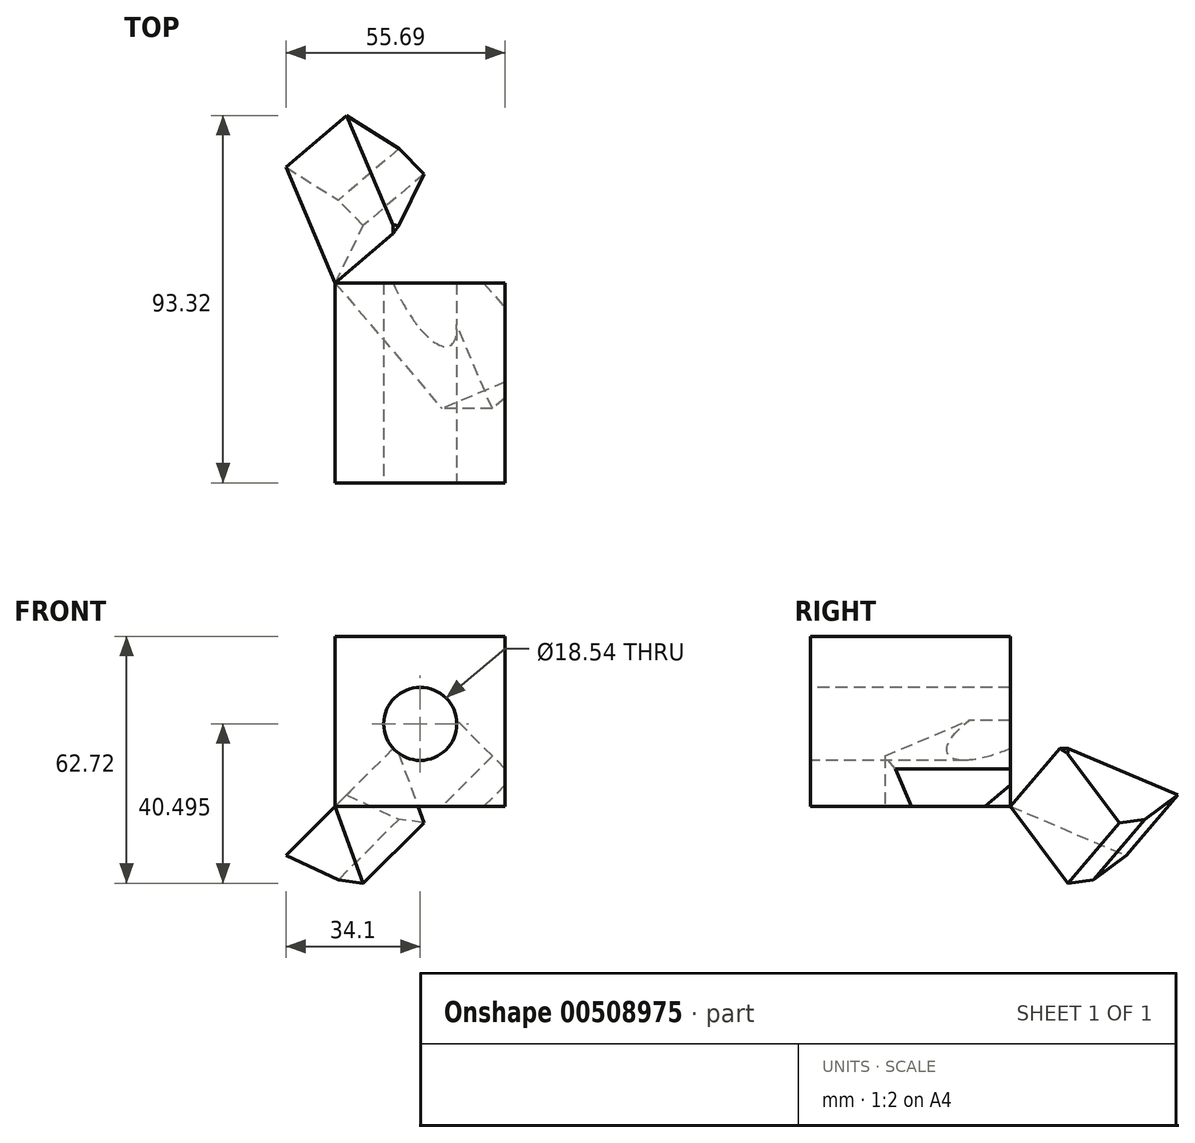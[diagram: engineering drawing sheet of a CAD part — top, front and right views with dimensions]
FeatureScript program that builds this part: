
annotation { "Feature Type Name" : "Feature", "Feature Type Description" : "" }
export const myFeature = defineFeature(function(context is Context, id is Id, definition is map)
    precondition{}
    {
        {
            var Q0;
            Q0=qCreatedBy(makeId("Front.planeOp"),FACE);
            var sketch = newSketch(context, id + "F0", { "sketchPlane" : qUnion([Q0])});
            skLineSegment(sketch, "E0.bottom", {"start": v(0, 0) * mm, "end": v(43.18, 0) * mm});
            skLineSegment(sketch, "E0.top", {"start": v(0, 43.18) * mm, "end": v(43.18, 43.18) * mm});
            skLineSegment(sketch, "E0.left", {"start": v(0, 0) * mm, "end": v(0, 43.18) * mm});
            skLineSegment(sketch, "E0.right", {"start": v(43.18, 0) * mm, "end": v(43.18, 43.18) * mm});
            skSolve(sketch);
        }
        {
            var Q0;
            Q0=makeQuery(id+"F0.imprint","IMPRINT",FACE,{"disambiguationData":[TD([[makeQuery(id+"F0.imprint","IMPRINT",EDGE,{"derivedFrom":sQuery(id+"F0.wireOp",EDGE,"E0.bottom")}),1.0]])]});
            extrude(context, id + "F1", {"entities" : qUnion([Q0]), "depth" : 50.8 * mm, "offsetDistance" : 25.4 * mm});
        }
        {
            var Q0;
            Q0=makeQuery(id+"F1.opExtrude","CAP_VERTEX",VERTEX,{"disambiguationData":[OSD([sQuery(id+"F0.wireOp",EDGE,"E0.bottom"),sQuery(id+"F0.wireOp",EDGE,"E0.right")])],"isStart":false});
            var Q1;
            Q1=makeQuery(id+"F1.opExtrude","CAP_VERTEX",VERTEX,{"disambiguationData":[OSD([sQuery(id+"F0.wireOp",EDGE,"E0.top"),sQuery(id+"F0.wireOp",EDGE,"E0.left")])],"isStart":false});
            var Q2;
            Q2=qCreatedBy(makeId("Origin.pointOp"),VERTEX);
            cPlane(context, id + "F2", {"entities" : qUnion([Q0, Q1, Q2]), "cplaneType" : CPlaneType.THREE_POINT, "offset" : 25.4 * mm, "oppositeDirection" : true, "width" : 152.4 * mm, "height" : 152.4 * mm});
        }
        {
            var Q0;
            Q0=qCreatedBy(id+"F2.planeOp",FACE);
            var sketch = newSketch(context, id + "F3", { "sketchPlane" : qUnion([Q0])});
            skLineSegment(sketch, "E1", {"start": v(-12.96, -13.84) * mm, "end": v(0, 0) * mm});
            skLineSegment(sketch, "E2", {"start": v(0, 0) * mm, "end": v(17.03, -18.86) * mm});
            skLineSegment(sketch, "E3", {"start": v(17.03, -18.86) * mm, "end": v(36.85, -5.4) * mm});
            skLineSegment(sketch, "E4", {"start": v(36.85, -5.4) * mm, "end": v(57.98, -14.18) * mm});
            skLineSegment(sketch, "E5", {"start": v(57.98, -14.18) * mm, "end": v(64.33, -5.59) * mm});
            skLineSegment(sketch, "E6.0", {"start": v(0, 0) * mm, "end": v(34.35, 0) * mm});
            skLineSegment(sketch, "E7.0", {"start": v(34.35, 0) * mm, "end": v(14.4, -27.97) * mm});
            skSolve(sketch);
        }
        {
            var Q0;
            Q0 = qSketchRegion(id + "F3", true);
            extrude(context, id + "F4", {"entities" : qUnion([Q0]), "operationType" : NewBodyOperationType.ADD, "depth" : 25.4 * mm, "offsetDistance" : 25.4 * mm});
        }
        {
            var Q0;
            Q0=makeQuery(id+"F4.opExtrude","CAP_VERTEX",VERTEX,{"disambiguationData":[OSD([sQuery(id+"F3.wireOp",EDGE,"E2"),sQuery(id+"F3.wireOp",EDGE,"E6.0")])],"isStart":false});
            var Q1;
            Q1=makeQuery(id+"F4.opExtrude","CAP_VERTEX",VERTEX,{"disambiguationData":[OSD([sQuery(id+"F3.wireOp",EDGE,"E6.0"),sQuery(id+"F3.wireOp",EDGE,"E7.0")])],"isStart":true});
            var Q2;
            Q2=makeQuery(id+"F1.opExtrude","CAP_VERTEX",VERTEX,{"disambiguationData":[OSD([sQuery(id+"F0.wireOp",EDGE,"E0.top"),sQuery(id+"F0.wireOp",EDGE,"E0.right")])],"isStart":true});
            cPlane(context, id + "F5", {"entities" : qUnion([Q0, Q1, Q2]), "cplaneType" : CPlaneType.THREE_POINT, "offset" : 25.4 * mm, "width" : 152.4 * mm, "height" : 152.4 * mm});
        }
        {
            var Q0;
            Q0=qCreatedBy(id+"F5.planeOp",FACE);
            var sketch = newSketch(context, id + "F6", { "sketchPlane" : qUnion([Q0])});
            skCircle(sketch, "E8", {"center": v(-22.34, 27.43) * mm, "radius": 12.7 * mm});
            skLineSegment(sketch, "E9.0", {"start": v(-32.74, 0) * mm, "end": v(-45.03, 38.85) * mm});
            skLineSegment(sketch, "E10.0", {"start": v(-12.3, 38.85) * mm, "end": v(-45.03, 38.85) * mm});
            skLineSegment(sketch, "E11", {"start": v(-45.03, 38.85) * mm, "end": v(-22.34, 27.43) * mm, "construction": true});
            skSolve(sketch);
        }
        {
            var Q0;
            {var subQ0=sQuery(id+"F6.wireOp",EDGE,"E10.0");var subQ1=sQuery(id+"F6.wireOp",EDGE,"E8");var subQ2=makeQuery(id+"F6.imprint","INTERSECT",VERTEX,{"disambiguationData":[OD(0.0)],"derivedFrom":[subQ1,subQ0]});Q0=makeQuery(id+"F6.imprint","IMPRINT",FACE,{"disambiguationData":[TD([[makeQuery(id+"F6.imprint","IMPRINT",EDGE,{"disambiguationData":[TD([[subQ2,1.0]])],"derivedFrom":subQ1}),1.0]])]});}
            extrude(context, id + "F7", {"entities" : qUnion([Q0]), "operationType" : NewBodyOperationType.REMOVE, "oppositeDirection" : true, "depth" : 24.38 * mm, "offsetDistance" : 25.4 * mm});
        }
        {
            var Q0;
            Q0=makeQuery(id+"F1.opExtrude","CAP_VERTEX",VERTEX,{"disambiguationData":[OSD([sQuery(id+"F0.wireOp",EDGE,"E0.bottom"),sQuery(id+"F0.wireOp",EDGE,"E0.right")])],"isStart":false});
            var Q1;
            Q1=qCreatedBy(makeId("Origin.pointOp"),VERTEX);
            var Q2;
            Q2=makeQuery(id+"F1.opExtrude","CAP_VERTEX",VERTEX,{"disambiguationData":[OSD([sQuery(id+"F0.wireOp",EDGE,"E0.top"),sQuery(id+"F0.wireOp",EDGE,"E0.right")])],"isStart":true});
            cPlane(context, id + "F8", {"entities" : qUnion([Q0, Q1, Q2]), "cplaneType" : CPlaneType.THREE_POINT, "offset" : 25.4 * mm, "width" : 152.4 * mm, "height" : 152.4 * mm});
        }
        {
            var Q0;
            Q0=qCreatedBy(id+"F8.planeOp",FACE);
            var sketch = newSketch(context, id + "F9", { "sketchPlane" : qUnion([Q0])});
            skLineSegment(sketch, "E12.bottom", {"start": v(37.27, 37.27) * mm, "end": v(0, 37.27) * mm});
            skLineSegment(sketch, "E12.top", {"start": v(37.27, 0) * mm, "end": v(0, 0) * mm});
            skLineSegment(sketch, "E12.left", {"start": v(37.27, 37.27) * mm, "end": v(37.27, 0) * mm});
            skLineSegment(sketch, "E12.right", {"start": v(0, 37.27) * mm, "end": v(0, 0) * mm});
            skLineSegment(sketch, "E13.bottom", {"start": v(37.27, 37.27) * mm, "end": v(53.2, 37.27) * mm});
            skLineSegment(sketch, "E13.top", {"start": v(37.27, 53.2) * mm, "end": v(53.2, 53.2) * mm});
            skLineSegment(sketch, "E13.left", {"start": v(37.27, 37.27) * mm, "end": v(37.27, 53.2) * mm});
            skLineSegment(sketch, "E13.right", {"start": v(53.2, 37.27) * mm, "end": v(53.2, 53.2) * mm});
            skSolve(sketch);
        }
        {
            var Q0;
            Q0=makeQuery(id+"F9.imprint","IMPRINT",FACE,{"disambiguationData":[TD([[makeQuery(id+"F9.imprint","IMPRINT",EDGE,{"derivedFrom":sQuery(id+"F9.wireOp",EDGE,"E12.bottom")}),1.0]])]});
            extrude(context, id + "F10", {"entities" : qUnion([Q0]), "operationType" : NewBodyOperationType.REMOVE, "oppositeDirection" : true, "depth" : 22.86 * mm, "offsetDistance" : 25.4 * mm});
        }
        {
            var Q0;
            Q0=makeQuery(id+"F1.opExtrude","CAP_FACE",FACE,{"disambiguationData":[OSD([sQuery(id+"F0.wireOp",EDGE,"E0.bottom"),sQuery(id+"F0.wireOp",EDGE,"E0.top"),sQuery(id+"F0.wireOp",EDGE,"E0.left"),sQuery(id+"F0.wireOp",EDGE,"E0.right")])],"isStart":false});
            var sketch = newSketch(context, id + "F11", { "sketchPlane" : qUnion([Q0])});
            skLineSegment(sketch, "E14", {"start": v(21.59, 43.18) * mm, "end": v(21.59, 20.96) * mm, "construction": true});
            skCircle(sketch, "E15", {"center": v(21.59, 20.96) * mm, "radius": 9.27 * mm});
            skSolve(sketch);
        }
        {
            var Q0;
            Q0=makeQuery(id+"F11.imprint","IMPRINT",FACE,{"disambiguationData":[TD([[makeQuery(id+"F11.imprint","IMPRINT",EDGE,{"derivedFrom":sQuery(id+"F11.wireOp",EDGE,"E15")}),1.0]])]});
            extrude(context, id + "F12", {"entities" : qUnion([Q0]), "operationType" : NewBodyOperationType.REMOVE, "oppositeDirection" : true, "depth" : 508 * mm, "offsetDistance" : 25.4 * mm});
        }
    });
